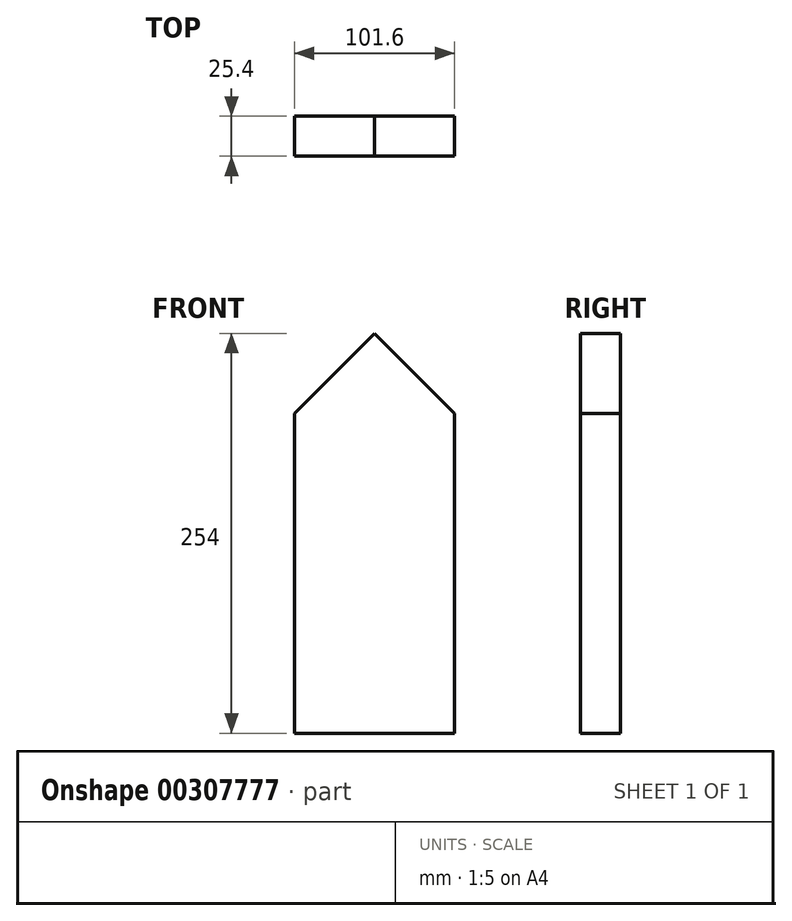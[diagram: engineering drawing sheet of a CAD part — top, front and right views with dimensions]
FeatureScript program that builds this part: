
annotation { "Feature Type Name" : "Feature", "Feature Type Description" : "" }
export const myFeature = defineFeature(function(context is Context, id is Id, definition is map)
    precondition{}
    {
        {
            var Q0;
            Q0=qCreatedBy(makeId("Front.planeOp"),FACE);
            var sketch = newSketch(context, id + "F0", { "sketchPlane" : qUnion([Q0])});
            skLineSegment(sketch, "E0.bottom", {"start": v(-64.15, 50.79) * mm, "end": v(37.45, 50.79) * mm});
            skLineSegment(sketch, "E0.top", {"start": v(-64.15, -152.41) * mm, "end": v(37.45, -152.41) * mm});
            skLineSegment(sketch, "E0.left", {"start": v(-64.15, 50.79) * mm, "end": v(-64.15, -152.41) * mm});
            skLineSegment(sketch, "E0.right", {"start": v(37.45, 50.79) * mm, "end": v(37.45, -152.41) * mm});
            skLineSegment(sketch, "E1", {"start": v(-64.15, 50.79) * mm, "end": v(-13.35, 101.59) * mm});
            skLineSegment(sketch, "E2", {"start": v(-13.35, 101.59) * mm, "end": v(37.45, 50.79) * mm});
            skSolve(sketch);
        }
        {
            var Q0;
            Q0=makeQuery(id+"F0.imprint","IMPRINT",FACE,{"disambiguationData":[TD([[makeQuery(id+"F0.imprint","IMPRINT",EDGE,{"derivedFrom":sQuery(id+"F0.wireOp",EDGE,"E0.bottom")}),-1.0]])]});
            var Q1;
            Q1=makeQuery(id+"F0.imprint","IMPRINT",FACE,{"disambiguationData":[TD([[makeQuery(id+"F0.imprint","IMPRINT",EDGE,{"derivedFrom":sQuery(id+"F0.wireOp",EDGE,"E0.bottom")}),1.0]])]});
            extrude(context, id + "F1", {"entities" : qUnion([Q0, Q1]), "depth" : 25.4 * mm});
        }
    });
